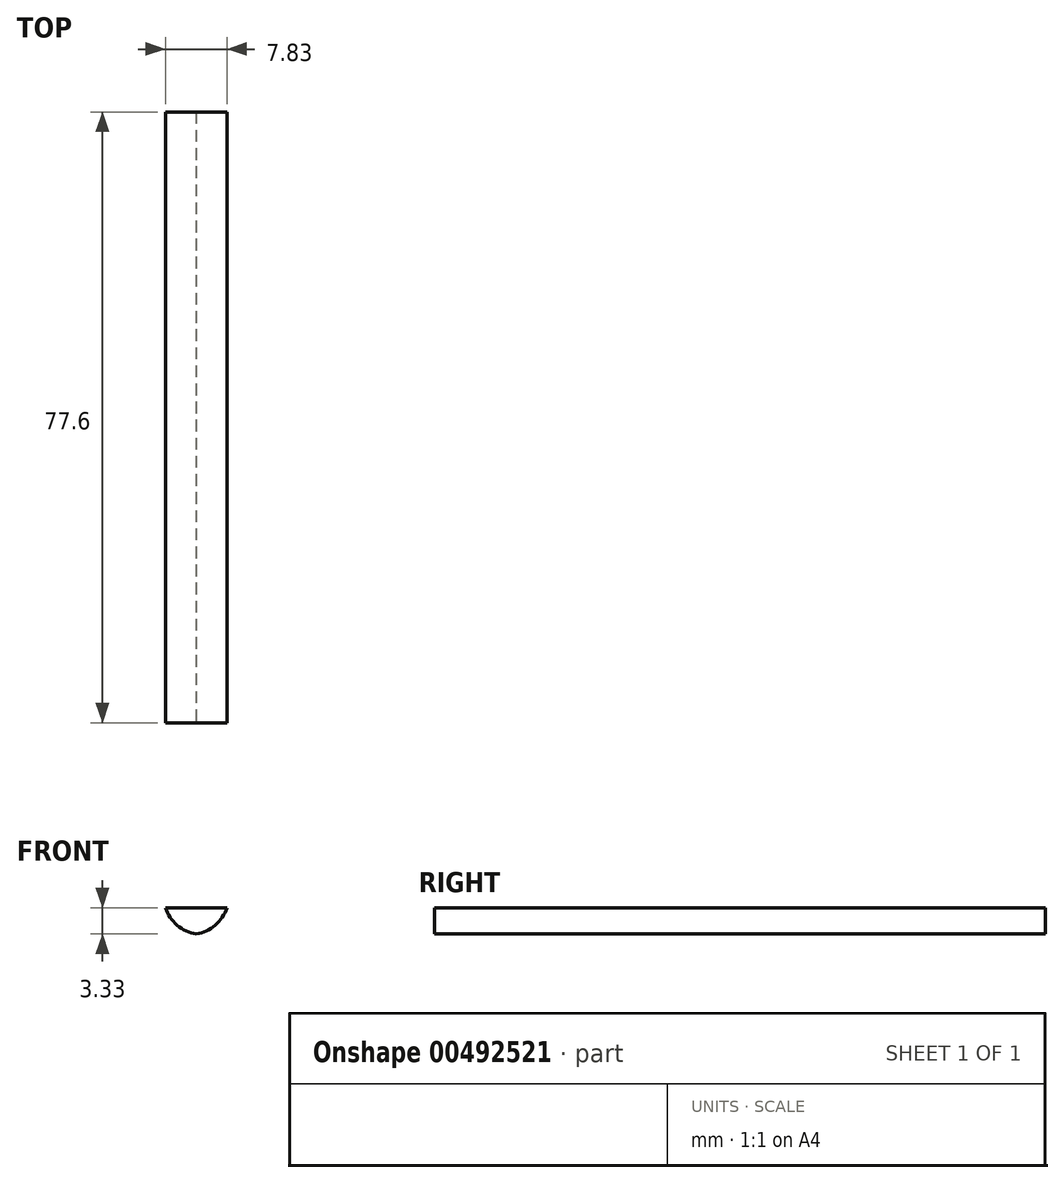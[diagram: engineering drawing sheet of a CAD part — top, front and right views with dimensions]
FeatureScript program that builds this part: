
annotation { "Feature Type Name" : "Feature", "Feature Type Description" : "" }
export const myFeature = defineFeature(function(context is Context, id is Id, definition is map)
    precondition{}
    {
        {
            var Q0;
            Q0=qCreatedBy(makeId("Top.planeOp"),FACE);
            var sketch = newSketch(context, id + "F0", { "sketchPlane" : qUnion([Q0])});
            skLineSegment(sketch, "E0.bottom", {"start": v(-39.14, 77.6) * mm, "end": v(-31.31, 77.6) * mm});
            skLineSegment(sketch, "E0.top", {"start": v(-39.14, 0) * mm, "end": v(-31.31, 0) * mm});
            skLineSegment(sketch, "E0.left", {"start": v(-39.14, 77.6) * mm, "end": v(-39.14, 0) * mm});
            skLineSegment(sketch, "E0.right", {"start": v(-31.31, 77.6) * mm, "end": v(-31.31, 0) * mm});
            skSolve(sketch);
        }
        {
            var Q0;
            Q0=makeQuery(id+"F0.imprint","IMPRINT",FACE,{"disambiguationData":[TD([[makeQuery(id+"F0.imprint","IMPRINT",EDGE,{"derivedFrom":sQuery(id+"F0.wireOp",EDGE,"E0.bottom")}),-1.0]])]});
            extrude(context, id + "F1", {"entities" : qUnion([Q0]), "depth" : 3.4 * mm});
        }
        {
            var Q0;
            Q0=makeQuery(id+"F1.opExtrude","CAP_EDGE",EDGE,{"disambiguationData":[OSD([sQuery(id+"F0.wireOp",EDGE,"E0.right")])],"isStart":true});
            var Q1;
            Q1=makeQuery(id+"F1.opExtrude","CAP_EDGE",EDGE,{"disambiguationData":[OSD([sQuery(id+"F0.wireOp",EDGE,"E0.left")])],"isStart":true});
            fillet(context, id + "F2", {"entities" : qUnion([Q0, Q1]), "radius" : 5 * mm, "tangentPropagation" : true, "allowEdgeOverflow" : false});
        }
    });
